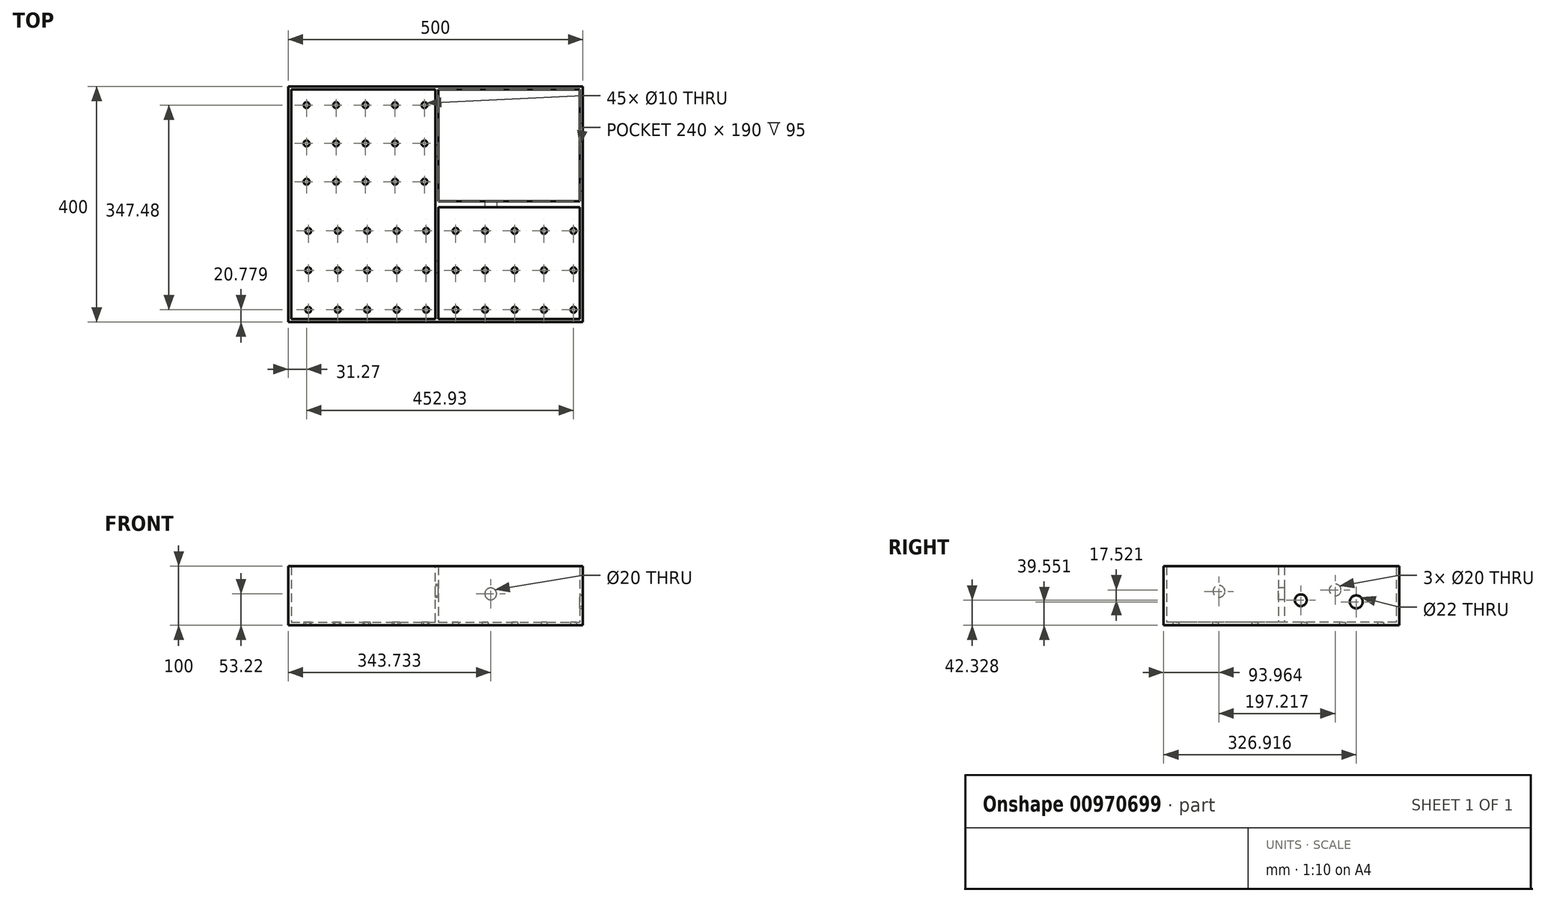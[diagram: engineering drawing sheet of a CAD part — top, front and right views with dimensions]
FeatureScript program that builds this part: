
annotation { "Feature Type Name" : "Feature", "Feature Type Description" : "" }
export const myFeature = defineFeature(function(context is Context, id is Id, definition is map)
    precondition{}
    {
        {
            var Q0;
            Q0=qCreatedBy(makeId("Top.planeOp"),FACE);
            var sketch = newSketch(context, id + "F0", { "sketchPlane" : qUnion([Q0])});
            skLineSegment(sketch, "E0.bottom", {"start": v(0, 0) * mm, "end": v(250, 0) * mm});
            skLineSegment(sketch, "E0.top", {"start": v(0, -400) * mm, "end": v(250, -400) * mm});
            skLineSegment(sketch, "E0.left", {"start": v(0, 0) * mm, "end": v(0, -400) * mm});
            skLineSegment(sketch, "E0.right", {"start": v(250, 0) * mm, "end": v(250, -400) * mm});
            skLineSegment(sketch, "E1.bottom", {"start": v(250, 0) * mm, "end": v(500, 0) * mm});
            skLineSegment(sketch, "E1.top", {"start": v(250, -200) * mm, "end": v(500, -200) * mm});
            skLineSegment(sketch, "E1.left", {"start": v(250, 0) * mm, "end": v(250, -200) * mm});
            skLineSegment(sketch, "E1.right", {"start": v(500, 0) * mm, "end": v(500, -200) * mm});
            skLineSegment(sketch, "E2.top", {"start": v(250, -400) * mm, "end": v(500, -400) * mm});
            skLineSegment(sketch, "E2.left", {"start": v(250, -200) * mm, "end": v(250, -400) * mm});
            skLineSegment(sketch, "E2.right", {"start": v(500, -200) * mm, "end": v(500, -400) * mm});
            skSolve(sketch);
        }
        {
            var Q0;
            {var subQ2=sQuery(id+"F0.wireOp",EDGE,"E1.top");Q0=makeQuery(id+"F0.imprint","IMPRINT",FACE,{"disambiguationData":[TD([[makeQuery(id+"F0.imprint","IMPRINT",EDGE,{"derivedFrom":subQ2}),-1.0]])]});}
            extrude(context, id + "F1", {"entities" : qUnion([Q0]), "depth" : 100 * mm, "offsetDistance" : 25 * mm});
        }
        {
            var Q0;
            Q0=makeQuery(id+"F1.opExtrude","CAP_FACE",FACE,{"disambiguationData":[OSD([sQuery(id+"F0.wireOp",EDGE,"E0.right"),sQuery(id+"F0.wireOp",EDGE,"E1.top"),sQuery(id+"F0.wireOp",EDGE,"E2.top"),sQuery(id+"F0.wireOp",EDGE,"E2.right")])],"isStart":false});
            shell(context, id + "F2", {"entities" : qUnion([Q0]), "thickness" : 5 * mm});
        }
        {
            var Q0;
            {var subQ0=sQuery(id+"F0.wireOp",EDGE,"E1.bottom");Q0=makeQuery(id+"F0.imprint","IMPRINT",FACE,{"disambiguationData":[TD([[makeQuery(id+"F0.imprint","IMPRINT",EDGE,{"derivedFrom":subQ0}),-1.0]])]});}
            extrude(context, id + "F3", {"entities" : qUnion([Q0]), "depth" : 100 * mm, "offsetDistance" : 25 * mm});
        }
        {
            var Q0;
            Q0=makeQuery(id+"F3.opExtrude","CAP_FACE",FACE,{"disambiguationData":[OSD([sQuery(id+"F0.wireOp",EDGE,"E0.right"),sQuery(id+"F0.wireOp",EDGE,"E1.bottom"),sQuery(id+"F0.wireOp",EDGE,"E1.top"),sQuery(id+"F0.wireOp",EDGE,"E1.right")])],"isStart":false});
            shell(context, id + "F4", {"entities" : qUnion([Q0]), "thickness" : 5 * mm});
        }
        {
            var Q0;
            {var subQ3=sQuery(id+"F0.wireOp",EDGE,"E0.bottom");Q0=makeQuery(id+"F0.imprint","IMPRINT",FACE,{"disambiguationData":[TD([[makeQuery(id+"F0.imprint","IMPRINT",EDGE,{"derivedFrom":subQ3}),-1.0]])]});}
            extrude(context, id + "F5", {"entities" : qUnion([Q0]), "operationType" : NewBodyOperationType.ADD, "depth" : 100 * mm, "offsetDistance" : 25 * mm});
        }
        {
            var Q0;
            {var subQ0=sQuery(id+"F0.wireOp",EDGE,"E0.right");var subQ1=sQuery(id+"F0.wireOp",EDGE,"E1.top");Q0=makeQuery(id+"F5.boolean.opBoolean","MERGE",FACE,{"derivedFrom":[makeQuery(id+"F1.opExtrude","CAP_FACE",FACE,{"disambiguationData":[OSD([subQ0,subQ1,sQuery(id+"F0.wireOp",EDGE,"E2.top"),sQuery(id+"F0.wireOp",EDGE,"E2.right")])],"isStart":false}),makeQuery(id+"F3.opExtrude","CAP_FACE",FACE,{"disambiguationData":[OSD([subQ0,sQuery(id+"F0.wireOp",EDGE,"E1.bottom"),subQ1,sQuery(id+"F0.wireOp",EDGE,"E1.right")])],"isStart":false}),makeQuery(id+"F5.opExtrude","CAP_FACE",FACE,{"disambiguationData":[OSD([sQuery(id+"F0.wireOp",EDGE,"E0.bottom"),sQuery(id+"F0.wireOp",EDGE,"E0.top"),sQuery(id+"F0.wireOp",EDGE,"E0.left"),subQ0])],"isStart":false})]});}
            shell(context, id + "F6", {"entities" : qUnion([Q0]), "thickness" : 5 * mm});
        }
        {
            var Q0;
            Q0=makeQuery(id+"F4.opShell","OFFSET_FACE",FACE,{"disambiguationData":[OSD([sQuery(id+"F0.wireOp",EDGE,"E0.right")])]});
            cPlane(context, id + "F7", {"entities" : qUnion([Q0]), "cplaneType" : CPlaneType.OFFSET, "offset" : 0 * mm, "width" : 150 * mm, "height" : 150 * mm});
        }
        {
            var Q0;
            Q0=qCreatedBy(id+"F7.planeOp",FACE);
            var sketch = newSketch(context, id + "F8", { "sketchPlane" : qUnion([Q0])});
            skCircle(sketch, "E3", {"center": v(-108.82, 59.85) * mm, "radius": 10 * mm});
            skCircle(sketch, "E4", {"center": v(-306.04, 57.38) * mm, "radius": 10 * mm});
            skSolve(sketch);
        }
        {
            var Q0;
            Q0=qSketchRegion(id+"F8",true);
            extrude(context, id + "F9", {"entities" : qUnion([Q0]), "operationType" : NewBodyOperationType.REMOVE, "oppositeDirection" : true, "depth" : 25 * mm, "offsetDistance" : 25 * mm});
        }
        {
            var Q0;
            Q0=makeQuery(id+"F2.opShell","OFFSET_FACE",FACE,{"disambiguationData":[OSD([sQuery(id+"F0.wireOp",EDGE,"E1.top")])]});
            cPlane(context, id + "F10", {"entities" : qUnion([Q0]), "cplaneType" : CPlaneType.OFFSET, "offset" : 0 * mm, "width" : 150 * mm, "height" : 150 * mm});
        }
        {
            var Q0;
            Q0=qCreatedBy(id+"F10.planeOp",FACE);
            var sketch = newSketch(context, id + "F11", { "sketchPlane" : qUnion([Q0])});
            skCircle(sketch, "E5", {"center": v(343.73, 53.22) * mm, "radius": 10 * mm});
            skSolve(sketch);
        }
        {
            var Q0;
            Q0=makeQuery(id+"F11.imprint","IMPRINT",FACE,{"disambiguationData":[TD([[makeQuery(id+"F11.imprint","IMPRINT",EDGE,{"derivedFrom":sQuery(id+"F11.wireOp",EDGE,"E5")}),1.0]])]});
            extrude(context, id + "F12", {"entities" : qUnion([Q0]), "operationType" : NewBodyOperationType.REMOVE, "oppositeDirection" : true, "depth" : 25 * mm, "offsetDistance" : 25 * mm});
        }
        {
            var Q0;
            {var subQ0=sQuery(id+"F0.wireOp",EDGE,"E0.right");var subQ1=sQuery(id+"F0.wireOp",EDGE,"E1.top");Q0=makeQuery(id+"F5.boolean.opBoolean","MERGE",FACE,{"derivedFrom":[makeQuery(id+"F1.opExtrude","CAP_FACE",FACE,{"disambiguationData":[OSD([subQ0,subQ1,sQuery(id+"F0.wireOp",EDGE,"E2.top"),sQuery(id+"F0.wireOp",EDGE,"E2.right")])],"isStart":true}),makeQuery(id+"F3.opExtrude","CAP_FACE",FACE,{"disambiguationData":[OSD([subQ0,sQuery(id+"F0.wireOp",EDGE,"E1.bottom"),subQ1,sQuery(id+"F0.wireOp",EDGE,"E1.right")])],"isStart":true}),makeQuery(id+"F5.opExtrude","CAP_FACE",FACE,{"disambiguationData":[OSD([sQuery(id+"F0.wireOp",EDGE,"E0.bottom"),sQuery(id+"F0.wireOp",EDGE,"E0.top"),sQuery(id+"F0.wireOp",EDGE,"E0.left"),subQ0])],"isStart":true})]});}
            cPlane(context, id + "F13", {"entities" : qUnion([Q0]), "cplaneType" : CPlaneType.OFFSET, "offset" : 0 * mm, "width" : 150 * mm, "height" : 150 * mm});
        }
        {
            var Q0;
            Q0=qCreatedBy(id+"F13.planeOp",FACE);
            var sketch = newSketch(context, id + "F14", { "sketchPlane" : qUnion([Q0])});
            skCircle(sketch, "E6", {"center": v(31.27, 31.74) * mm, "radius": 5 * mm});
            skCircle(sketch, "E7", {"center": v(484.2, 379.22) * mm, "radius": 5 * mm});
            skCircle(sketch, "E8.0.1.0", {"center": v(484.2, 312.22) * mm, "radius": 5 * mm});
            skCircle(sketch, "E8.0.2.0", {"center": v(484.2, 245.22) * mm, "radius": 5 * mm});
            skCircle(sketch, "E8.1.0.0", {"center": v(434.2, 379.22) * mm, "radius": 5 * mm});
            skCircle(sketch, "E8.1.1.0", {"center": v(434.2, 312.22) * mm, "radius": 5 * mm});
            skCircle(sketch, "E8.1.2.0", {"center": v(434.2, 245.22) * mm, "radius": 5 * mm});
            skCircle(sketch, "E8.2.0.0", {"center": v(384.2, 379.22) * mm, "radius": 5 * mm});
            skCircle(sketch, "E8.2.1.0", {"center": v(384.2, 312.22) * mm, "radius": 5 * mm});
            skCircle(sketch, "E8.2.2.0", {"center": v(384.2, 245.22) * mm, "radius": 5 * mm});
            skCircle(sketch, "E8.3.0.0", {"center": v(334.2, 379.22) * mm, "radius": 5 * mm});
            skCircle(sketch, "E8.3.1.0", {"center": v(334.2, 312.22) * mm, "radius": 5 * mm});
            skCircle(sketch, "E8.3.2.0", {"center": v(334.2, 245.22) * mm, "radius": 5 * mm});
            skCircle(sketch, "E8.4.0.0", {"center": v(284.2, 379.22) * mm, "radius": 5 * mm});
            skCircle(sketch, "E8.4.1.0", {"center": v(284.2, 312.22) * mm, "radius": 5 * mm});
            skCircle(sketch, "E8.4.2.0", {"center": v(284.2, 245.22) * mm, "radius": 5 * mm});
            skCircle(sketch, "E8.5.0.0", {"center": v(234.2, 379.22) * mm, "radius": 5 * mm});
            skCircle(sketch, "E8.5.1.0", {"center": v(234.2, 312.22) * mm, "radius": 5 * mm});
            skCircle(sketch, "E8.5.2.0", {"center": v(234.2, 245.22) * mm, "radius": 5 * mm});
            skCircle(sketch, "E8.6.0.0", {"center": v(184.2, 379.22) * mm, "radius": 5 * mm});
            skCircle(sketch, "E8.6.1.0", {"center": v(184.2, 312.22) * mm, "radius": 5 * mm});
            skCircle(sketch, "E8.6.2.0", {"center": v(184.2, 245.22) * mm, "radius": 5 * mm});
            skCircle(sketch, "E8.7.0.0", {"center": v(134.2, 379.22) * mm, "radius": 5 * mm});
            skCircle(sketch, "E8.7.1.0", {"center": v(134.2, 312.22) * mm, "radius": 5 * mm});
            skCircle(sketch, "E8.7.2.0", {"center": v(134.2, 245.22) * mm, "radius": 5 * mm});
            skCircle(sketch, "E8.8.0.0", {"center": v(84.2, 379.22) * mm, "radius": 5 * mm});
            skCircle(sketch, "E8.8.1.0", {"center": v(84.2, 312.22) * mm, "radius": 5 * mm});
            skCircle(sketch, "E8.8.2.0", {"center": v(84.2, 245.22) * mm, "radius": 5 * mm});
            skCircle(sketch, "E8.9.0.0", {"center": v(34.2, 379.22) * mm, "radius": 5 * mm});
            skCircle(sketch, "E8.9.1.0", {"center": v(34.2, 312.22) * mm, "radius": 5 * mm});
            skCircle(sketch, "E8.9.2.0", {"center": v(34.2, 245.22) * mm, "radius": 5 * mm});
            skLineSegment(sketch, "E8.direction1", {"start": v(484.2, 379.22) * mm, "end": v(434.2, 379.22) * mm, "construction": true});
            skLineSegment(sketch, "E8.direction2", {"start": v(484.2, 379.22) * mm, "end": v(484.2, 312.22) * mm, "construction": true});
            skCircle(sketch, "E9.0.1.0", {"center": v(31.27, 96.74) * mm, "radius": 5 * mm});
            skCircle(sketch, "E9.0.2.0", {"center": v(31.27, 161.74) * mm, "radius": 5 * mm});
            skCircle(sketch, "E9.1.0.0", {"center": v(81.27, 31.74) * mm, "radius": 5 * mm});
            skCircle(sketch, "E9.1.1.0", {"center": v(81.27, 96.74) * mm, "radius": 5 * mm});
            skCircle(sketch, "E9.1.2.0", {"center": v(81.27, 161.74) * mm, "radius": 5 * mm});
            skCircle(sketch, "E9.2.0.0", {"center": v(131.27, 31.74) * mm, "radius": 5 * mm});
            skCircle(sketch, "E9.2.1.0", {"center": v(131.27, 96.74) * mm, "radius": 5 * mm});
            skCircle(sketch, "E9.2.2.0", {"center": v(131.27, 161.74) * mm, "radius": 5 * mm});
            skCircle(sketch, "E9.3.0.0", {"center": v(181.27, 31.74) * mm, "radius": 5 * mm});
            skCircle(sketch, "E9.3.1.0", {"center": v(181.27, 96.74) * mm, "radius": 5 * mm});
            skCircle(sketch, "E9.3.2.0", {"center": v(181.27, 161.74) * mm, "radius": 5 * mm});
            skCircle(sketch, "E9.4.0.0", {"center": v(231.27, 31.74) * mm, "radius": 5 * mm});
            skCircle(sketch, "E9.4.1.0", {"center": v(231.27, 96.74) * mm, "radius": 5 * mm});
            skCircle(sketch, "E9.4.2.0", {"center": v(231.27, 161.74) * mm, "radius": 5 * mm});
            skLineSegment(sketch, "E9.direction1", {"start": v(31.27, 31.74) * mm, "end": v(81.27, 31.74) * mm, "construction": true});
            skLineSegment(sketch, "E9.direction2", {"start": v(31.27, 31.74) * mm, "end": v(31.27, 96.74) * mm, "construction": true});
            skSolve(sketch);
        }
        {
            var Q0;
            Q0=qSketchRegion(id+"F14",true);
            extrude(context, id + "F15", {"entities" : qUnion([Q0]), "operationType" : NewBodyOperationType.REMOVE, "oppositeDirection" : true, "depth" : 25 * mm, "offsetDistance" : 25 * mm});
        }
        {
            var Q0;
            Q0=makeQuery(id+"F5.boolean.opBoolean","MERGE",FACE,{"derivedFrom":[makeQuery(id+"F1.opExtrude","SWEPT_FACE",FACE,{"disambiguationData":[OSD([sQuery(id+"F0.wireOp",EDGE,"E2.right")])]}),makeQuery(id+"F3.opExtrude","SWEPT_FACE",FACE,{"disambiguationData":[OSD([sQuery(id+"F0.wireOp",EDGE,"E1.right")])]})]});
            cPlane(context, id + "F16", {"entities" : qUnion([Q0]), "cplaneType" : CPlaneType.OFFSET, "offset" : 0 * mm, "width" : 150 * mm, "height" : 150 * mm});
        }
        {
            var Q0;
            Q0=qCreatedBy(id+"F16.planeOp",FACE);
            var sketch = newSketch(context, id + "F17", { "sketchPlane" : qUnion([Q0])});
            skCircle(sketch, "E10", {"center": v(-167.15, 42.33) * mm, "radius": 10 * mm});
            skSolve(sketch);
        }
        {
            var Q0;
            Q0=makeQuery(id+"F17.imprint","IMPRINT",FACE,{"disambiguationData":[TD([[makeQuery(id+"F17.imprint","IMPRINT",EDGE,{"derivedFrom":sQuery(id+"F17.wireOp",EDGE,"E10")}),1.0]])]});
            extrude(context, id + "F18", {"entities" : qUnion([Q0]), "operationType" : NewBodyOperationType.REMOVE, "oppositeDirection" : true, "depth" : 25 * mm, "offsetDistance" : 25 * mm});
        }
        {
            var Q0;
            Q0=qCreatedBy(id+"F16.planeOp",FACE);
            var sketch = newSketch(context, id + "F19", { "sketchPlane" : qUnion([Q0])});
            skCircle(sketch, "E11", {"center": v(-73.08, 39.55) * mm, "radius": 11 * mm});
            skSolve(sketch);
        }
        {
            var Q0;
            Q0=qSketchRegion(id+"F19",true);
            extrude(context, id + "F20", {"entities" : qUnion([Q0]), "operationType" : NewBodyOperationType.REMOVE, "oppositeDirection" : true, "depth" : 25 * mm, "offsetDistance" : 25 * mm});
        }
    });
